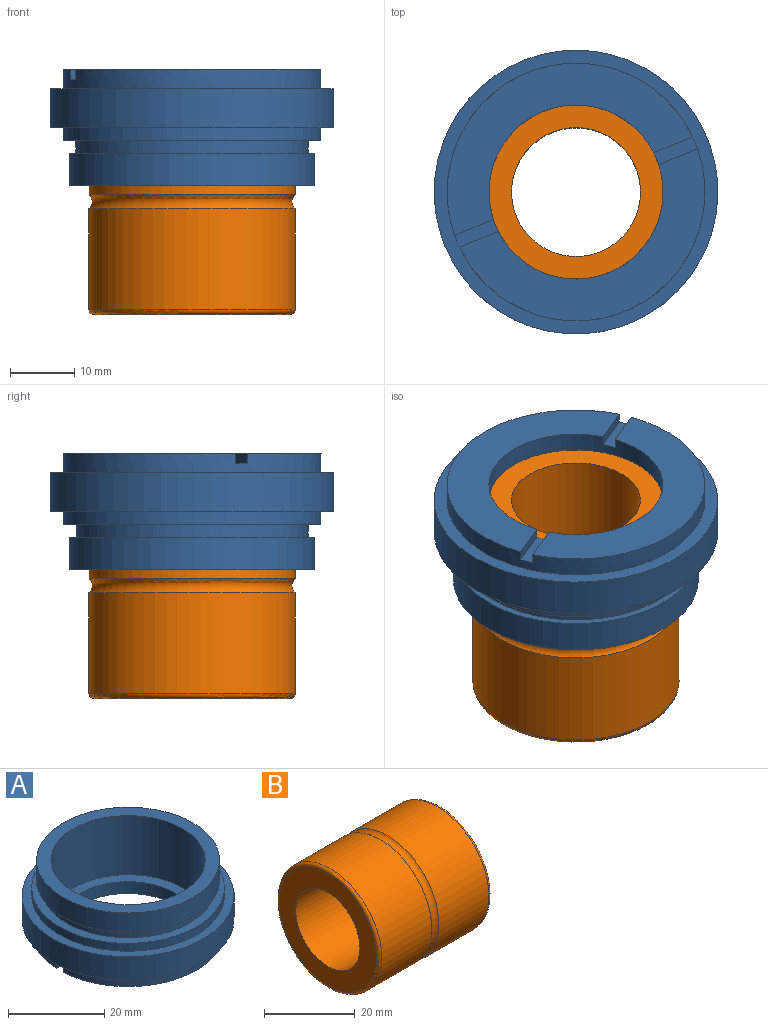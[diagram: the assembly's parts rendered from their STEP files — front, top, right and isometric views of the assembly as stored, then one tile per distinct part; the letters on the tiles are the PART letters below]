
ASSEMBLY  parts=2 mates=1
PART A: 21 faces, bbox 44x44x18 mm
  f0: cylinder r=13.5mm len=27mm, axis (0,0,1), area 248.5mm2, adj f1,f2,f14,f15,f16,f17,f18,f19
  f1: plane 39.95x19mm, normal (0,0,-1), area 329mm2, adj f0,f3,f15,f19
  f2: plane 39.95x19mm, normal (0,0,-1), area 329mm2, adj f0,f3,f16,f18
  f3: cylinder r=20mm len=40mm, axis (0,0,1), area 371mm2, adj f1,f2,f4,f15,f16,f17,f18,f19
  f4: plane 44x44mm, normal (0,0,-1), area 263.9mm2, adj f3,f5
  f5: cylinder r=22mm len=44mm, axis (0,0,1), area 829.4mm2, adj f4,f6
  f6: plane 44x44mm, normal (0,0,1), area 263.9mm2, adj f5,f7
  f7: cylinder r=20mm len=40mm, axis (0,0,1), area 251.3mm2, adj f6,f8
  f8: plane 40x40mm, normal (0,0,1), area 238.8mm2, adj f7,f9
  f9: cylinder r=18mm len=36mm, axis (0,0,1), area 226.2mm2, adj f8,f10
  f10: plane 38x38mm, normal (0,0,-1), area 116.2mm2, adj f9,f11
  f11: cylinder r=19mm len=38mm, axis (0,0,1), area 596.9mm2, adj f10,f12
  f12: plane 38x38mm, normal (0,0,1), area 329.9mm2, adj f11,f13
  f13: cylinder r=16mm len=32mm, axis (0,0,1), area 1508mm2, adj f12,f14
  f14: plane 32x32mm, normal (0,0,1), area 231.7mm2, adj f0,f13
  f15: plane 6.51x1.5mm, normal (0,-1,0), area 9.8mm2, adj f0,f1,f3,f17
  f16: plane 6.51x1.5mm, normal (0,1,0), area 9.8mm2, adj f0,f2,f3,f17
  f17: plane 6.54x2mm, normal (0,0,-1), area 13mm2, adj f0,f3,f15,f16
  f18: plane 6.51x1.5mm, normal (0,1,0), area 9.8mm2, adj f0,f2,f3,f20
  f19: plane 6.51x1.5mm, normal (0,-1,0), area 9.8mm2, adj f0,f1,f3,f20
  f20: plane 6.54x2mm, normal (0,0,-1), area 13mm2, adj f0,f3,f18,f19
PART B: 8 faces, bbox 35x36.8x36.8 mm
  f0: plane 30.4x30.4mm, normal (-1,0,0), area 411.7mm2, adj f1,f2
  f1: cylinder r=10mm len=35mm, axis (1,0,0), area 2199.1mm2, adj f0,f3
  f2: torus R=15.2mm, axis (1,0,0), area 124mm2, adj f0,f4
  f3: plane 30.4x30.4mm, normal (1,0,0), area 411.6mm2, adj f1,f5
  f4: cylinder r=16mm len=32mm, axis (1,0,0), area 1566.5mm2, adj f2,f7
  f5: torus R=15.2mm, axis (1,0,0), area 124mm2, adj f3,f6
  f6: cylinder r=16mm len=32mm, axis (1,0,0), area 1566.5mm2, adj f5,f7
  f7: torus R=17mm, axis (1,0,0), area 248.4mm2, adj f4,f6
PLACE A rot(axis=(0.2,-0.98,0),180deg) t=(0,0,6)mm
PLACE B rot(axis=(-0.19,0.96,0.19),92.2deg) t=(0,0,3)mm
MATE revolute B.f1 <-> A.f0  axis (0,0,1) through (0,0,3)mm
